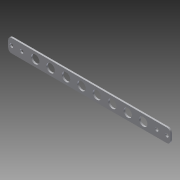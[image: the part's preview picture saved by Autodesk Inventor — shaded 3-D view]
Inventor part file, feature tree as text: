
AUTODESK INVENTOR PART (.ipt)
format: ipt  version: 2014 SP1 (Build 180222100, 222)  size: 169,984 bytes
history: native  units: in
note: dims shown in document units (in); Inventor stores cm internally (conversion verified against a paired STEP export)
features: reference x2, other x2, sketch x1, sheet_metal_op x1, chamfer x1
ambient origin geometry x8: Origin, YZ Plane, XZ Plane, XY Plane, X Axis, Y Axis, Z Axis, Center Point
bodies: Solid1 (feature_tree)
feature tree (7):
  sketch  "Sketch1"  dims[d1=1.0in d2=0.5in d3=0.12in d32=0.25in d33=0.625in d35=11.9901in d36=2.0in d37=3.1496in d39=1.1414in d40=0.3937in d42=1.0in]
  sheet_metal_op  "Face1"
  chamfer  "Corner Round1"
  reference  "Reference1"
  reference  "Reference2"
  other  "Plate1"
  other  "Definition1"
